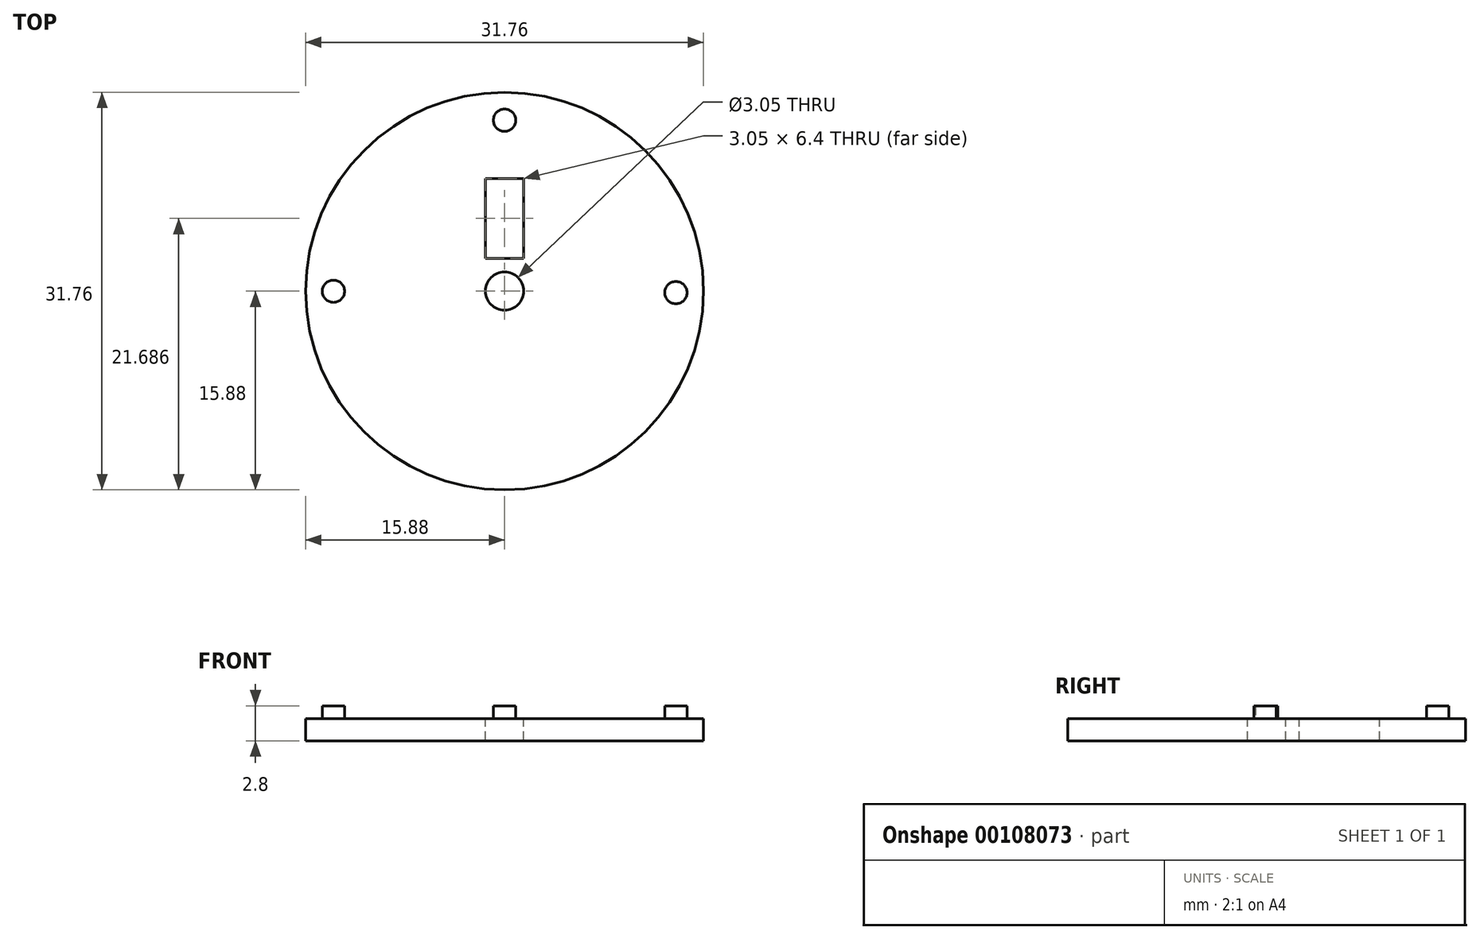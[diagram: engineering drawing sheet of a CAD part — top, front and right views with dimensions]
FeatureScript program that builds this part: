
annotation { "Feature Type Name" : "Feature", "Feature Type Description" : "" }
export const myFeature = defineFeature(function(context is Context, id is Id, definition is map)
    precondition{}
    {
        {
            var Q0;
            Q0=qCreatedBy(makeId("Top.planeOp"),FACE);
            var sketch = newSketch(context, id + "F0", { "sketchPlane" : qUnion([Q0])});
            skCircle(sketch, "E0", {"center": v(0, 0) * mm, "radius": 15.88 * mm});
            skSolve(sketch);
        }
        {
            var Q0;
            Q0=qSketchRegion(id+"F0",true);
            extrude(context, id + "F1", {"entities" : qUnion([Q0]), "oppositeDirection" : true, "depth" : 1.78 * mm});
        }
        {
            var Q0;
            Q0=makeQuery(id+"F1.opExtrude","CAP_FACE",FACE,{"disambiguationData":[OSD([sQuery(id+"F0.wireOp",EDGE,"E0")])],"isStart":true});
            var sketch = newSketch(context, id + "F2", { "sketchPlane" : qUnion([Q0])});
            skCircle(sketch, "E1", {"center": v(0, 0) * mm, "radius": 12.7 * mm});
            skSolve(sketch);
        }
        {
            var Q0;
            Q0=makeQuery(id+"F2.imprint","IMPRINT",FACE,{"disambiguationData":[TD([[makeQuery(id+"F2.imprint","IMPRINT",EDGE,{"derivedFrom":sQuery(id+"F2.wireOp",EDGE,"E1")}),-1.0]])]});
            var sketch = newSketch(context, id + "F3", { "sketchPlane" : qUnion([Q0])});
            skCircle(sketch, "E2", {"center": v(0, 13.65) * mm, "radius": 0.89 * mm});
            skCircle(sketch, "E3", {"center": v(-13.66, -0.02) * mm, "radius": 0.89 * mm});
            skCircle(sketch, "E4", {"center": v(13.67, -0.12) * mm, "radius": 0.89 * mm});
            skSolve(sketch);
        }
        {
            var Q0;
            Q0=qSketchRegion(id+"F3",true);
            extrude(context, id + "F4", {"entities" : qUnion([Q0]), "operationType" : NewBodyOperationType.ADD, "depth" : 1.02 * mm});
        }
        {
            var Q0;
            Q0=makeQuery(id+"F2.imprint","IMPRINT",FACE,{"disambiguationData":[TD([[makeQuery(id+"F2.imprint","IMPRINT",EDGE,{"derivedFrom":sQuery(id+"F2.wireOp",EDGE,"E1")}),-1.0]])]});
            var sketch = newSketch(context, id + "F5", { "sketchPlane" : qUnion([Q0])});
            skCircle(sketch, "E5", {"center": v(0, 0) * mm, "radius": 1.52 * mm});
            skLineSegment(sketch, "E6.bottom", {"start": v(1.52, 2.6) * mm, "end": v(-1.52, 2.6) * mm});
            skLineSegment(sketch, "E6.top", {"start": v(1.52, 9) * mm, "end": v(-1.52, 9) * mm});
            skLineSegment(sketch, "E6.left", {"start": v(1.52, 2.6) * mm, "end": v(1.52, 9) * mm});
            skLineSegment(sketch, "E6.right", {"start": v(-1.52, 2.6) * mm, "end": v(-1.52, 9) * mm});
            skPoint(sketch, "E6.middle", {"position": v(0, 5.8) * mm});
            skSolve(sketch);
        }
        {
            var Q0;
            Q0 = qSketchRegion(id + "F5", true);
            extrude(context, id + "F6", {"entities" : qUnion([Q0]), "operationType" : NewBodyOperationType.REMOVE, "oppositeDirection" : true, "depth" : 2.22 * mm});
        }
    });
